# Revit family: TH4090001_Griferia teleducha Thames
name_source: partatom
category: Plumbing Fixtures
units: mm (PartAtom-declared; Revit-internal decimal feet)

## family parameters
Always vertical = Yes
Cut with Voids When Loaded = No
Host = Wall
OmniClass Number = 23.31.17.00
OmniClass Title = Showers
Part Type = Normal
Room Calculation Point = No
Round Connector Dimension = Use Diameter
Shared = No

## types (1)
- Type 1
    Alto = 261 mm
    Altura ducha = 1200 mm  [stored 3.93701 ft]
    Ancho = 110 mm  [stored 0.360892 ft]
    Capacidad de flujo = A 80 psi 9.3 L/min
    Creado por = BIMBAU
    Default Elevation = 0 mm  [stored 0 ft]
    Description = La teleducha Thames es de tamaño medio y cuenta con la sistema MultiFlow. Ofrece mayor relajación gracias a sus diferentes tipos de chorro, con selector de funciones tipo palanca para una fácil operación.
Tiene un soporte ajustable que permite posicionar la teleducha en la posición ideal para uso como regadera; además, es de fácil limpieza gracias a las salidas de agua flexibles que evitan taponamientos.
    Dimensiones generales del producto = 52 x 270 x160 mm
    Fecha de creación = 06/07/2021
    Garantía = 30 años - 2 años Cromado
    Incluye = Cuerpo - manguera de 1.50 m
    Manufacturer = Corona
    Model = TH4090001_Grifería teleducha Thames
    No incluye = Desviador
    Normatividad = NTC 1644
    Peso neto = 476 g. - 1.04 lb
    Presión máxima recomendada = 125 psi ( 860 kPa)
    Presión mínima recomendada = 20 psi (140 kPa)
    Profundidad = 64 mm  [stored 0.209974 ft]
    Recubrimientos = Resistencia a la corrosión, pelado y decoloración por agua.
    Temperatura de uso = 5 °C a 71 °C
    Tipo de chorro = Tipo lluvia - Hidromasaje
    Tipo de regadera = Con funciones regadera con brazo
    URL = https://corona.co
    Uso = Residencial

note: [stored X ft] marks values corroborated as IEEE doubles in the binary element streams (Revit-internal decimal feet)

## geometry (parser evidence)
native form markers: Sweep x6
no freeform markers — native parametric forms only
